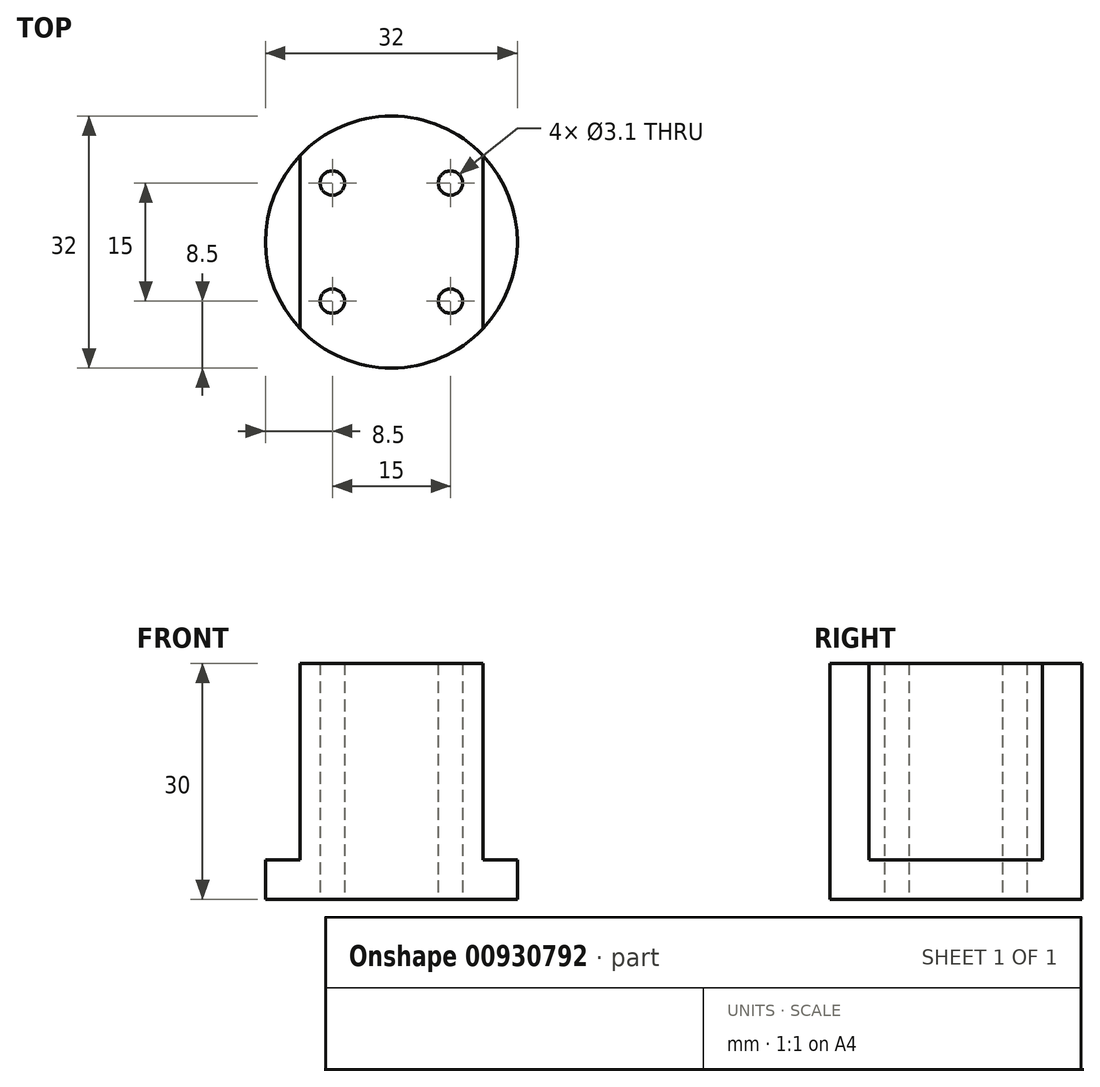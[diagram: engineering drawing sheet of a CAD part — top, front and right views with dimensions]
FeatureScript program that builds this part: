
annotation { "Feature Type Name" : "Feature", "Feature Type Description" : "" }
export const myFeature = defineFeature(function(context is Context, id is Id, definition is map)
    precondition{}
    {
        {
            var Q0;
            Q0=qCreatedBy(makeId("Top.planeOp"),FACE);
            var sketch = newSketch(context, id + "F0", { "sketchPlane" : qUnion([Q0])});
            skCircle(sketch, "E0", {"center": v(0, 0) * mm, "radius": 16 * mm});
            skLineSegment(sketch, "E1", {"start": v(-11.62, 11) * mm, "end": v(-11.62, -11) * mm});
            skLineSegment(sketch, "E2", {"start": v(11.62, -11) * mm, "end": v(11.62, 11) * mm});
            skLineSegment(sketch, "E3.bottom", {"start": v(7.5, -7.5) * mm, "end": v(-7.5, -7.5) * mm});
            skLineSegment(sketch, "E3.top", {"start": v(7.5, 7.5) * mm, "end": v(-7.5, 7.5) * mm});
            skLineSegment(sketch, "E3.left", {"start": v(7.5, -7.5) * mm, "end": v(7.5, 7.5) * mm});
            skLineSegment(sketch, "E3.right", {"start": v(-7.5, -7.5) * mm, "end": v(-7.5, 7.5) * mm});
            skCircle(sketch, "E4", {"center": v(-7.5, 7.5) * mm, "radius": 1.55 * mm});
            skCircle(sketch, "E5", {"center": v(7.5, 7.5) * mm, "radius": 1.55 * mm});
            skCircle(sketch, "E6", {"center": v(7.5, -7.5) * mm, "radius": 1.55 * mm});
            skCircle(sketch, "E7", {"center": v(-7.5, -7.5) * mm, "radius": 1.55 * mm});
            skSolve(sketch);
        }
        {
            var Q0;
            {var subQ0=sQuery(id+"F0.wireOp",EDGE,"E1");Q0=makeQuery(id+"F0.imprint","IMPRINT",FACE,{"disambiguationData":[TD([[makeQuery(id+"F0.imprint","IMPRINT",EDGE,{"derivedFrom":subQ0}),1.0]])]});}
            var Q1;
            {var subQ5=sQuery(id+"F0.wireOp",EDGE,"E6");var subQ10=sQuery(id+"F0.wireOp",EDGE,"E3.bottom");var subQ15=makeQuery(id+"F0.imprint","INTERSECT",VERTEX,{"derivedFrom":[subQ10,subQ5]});Q1=makeQuery(id+"F0.imprint","IMPRINT",FACE,{"disambiguationData":[TD([[makeQuery(id+"F0.imprint","IMPRINT",EDGE,{"disambiguationData":[TD([[subQ15,-1.0]])],"derivedFrom":subQ10}),-1.0]])]});}
            extrude(context, id + "F1", {"entities" : qUnion([Q0, Q1]), "depth" : 30 * mm, "offsetDistance" : 25 * mm});
        }
        {
            var Q0;
            {var subQ0=sQuery(id+"F0.wireOp",EDGE,"E1");Q0=makeQuery(id+"F0.imprint","IMPRINT",FACE,{"disambiguationData":[TD([[makeQuery(id+"F0.imprint","IMPRINT",EDGE,{"derivedFrom":subQ0}),-1.0]])]});}
            var Q1;
            {var subQ0=sQuery(id+"F0.wireOp",EDGE,"E2");Q1=makeQuery(id+"F0.imprint","IMPRINT",FACE,{"disambiguationData":[TD([[makeQuery(id+"F0.imprint","IMPRINT",EDGE,{"derivedFrom":subQ0}),-1.0]])]});}
            extrude(context, id + "F2", {"entities" : qUnion([Q0, Q1]), "operationType" : NewBodyOperationType.ADD, "depth" : 5 * mm, "offsetDistance" : 25 * mm});
        }
    });
